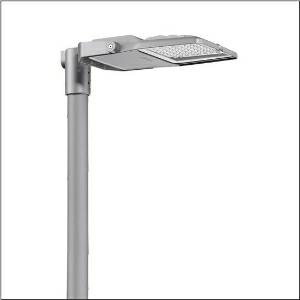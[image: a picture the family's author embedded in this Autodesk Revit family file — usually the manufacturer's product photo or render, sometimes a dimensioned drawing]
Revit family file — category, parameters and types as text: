
# Revit family: floodlight_fl_21_iq_mini___pl64_5xa7771b4e3a_3408
name_source: partatom
category: Lighting Fixtures
units: mm (PartAtom-declared; Revit-internal decimal feet)

## family parameters
Cut with Voids When Loaded = No
Host = Face
Light Source = No
Part Type = Normal
Room Calculation Point = No
Round Connector Dimension = Use Diameter
Shared = No

## types (1)
- --- (1 x LED, 6270 lm, 45.5 W, 4000K)
    Apparent Load = 46 VA
    CIE Flux Codes = 28 80 98 100 100
    Color Rendering = 70
    Color Temperature = 4000K
    Default Elevation = 1800 mm
    Description = Floodlight FL 21 iQ mini, floodlight, primary light control with lens, of PMMA, primary optical cover: protective disc, of toughened safety glass, transparent, light distribution: PL64, light emission: direct distribution, installation type: surface-mounted, LED, High Power LED, rated luminous flux: 6.270lm, luminous efficacy: 138lm/W, light colour: 740, colour temperature: 4000K, control gear: iQ Comfort/DALI, control: Auto-Match, Temp-Guard, Lumen-Switch, Night-Set, Smart-Wire, Light-Fading, Desk-Remote (wireless, voltage-free reading and setting of iQ features in the workshop via application-optimized NFC function/RFID function), optimised constant luminous flux control (CLO 2.0), with terminal, 6-pole, mains connection: 220..240V, AC, 50/60Hz, start of lifetime: 46W, end of service life: 48W, reduction: 22W, luminaire housing, of diecast aluminium, powder-coated, Siteco® metallic grey (DB 702S), corrosivity category C5 mid according to DIN EN ISO 12944, suitable for swimming pools, chlorine-resistant, sealing non-destructively replaceable, please order mast flange separately, mast bracket, of steel, galvanised, powder-coated, Siteco® metallic grey (DB 702S), protection rating (complete): IP66, insulation class (complete): insulation class II (safety insulation), certification: CE, ENEC, VDE, protection symbol: D, impact resistance: IK08, permissible operating ambient temperature: -40..+40°C, permissible operating ambient temperature for outdoor applications: -40..+50°C, standard: DIN EN 12944, LABS conformity tested according to VDMA 24364:2018-05, packaging unit: 1 piece

Light Distribution: PL64
    Height = 70 mm
    Lamp = 1 x LED
    Lamp Light Flux = 6270 lm
    Lamp Power = 45.5 W
    Lamp count = 1
    Length = 485 mm
    Luminous efficacy = 138 lm/W
    Manufacturer = Siteco
    ModVariant = No
    Model = 5XA7771B4E3A
    Number of Poles = 1
    OnlyDefault = Yes
    Power Factor = 1
    Product Name = Floodlight FL 21 iQ mini | PL64
    Product group = floodlight | pylon annexe
    ProductGroupID = 6200
    Protection Class = Protection class II
    Protection Degree = IP 66
    RLX_Detail_Level = 1
    RLX_Emergency_Light_Flux = 0 lm
    RLX_Emergency_Type = 0
    RLX_Emergency_Type_DB = No
    RlxData = <blob elided: 101345 chars, md5=1d864b85>
    Socket = socket
    Standby Power = 0 W
    System Light Flux = 6270 lm
    System Power = 46 W
    Type Comments = factory setting: luminous flux: 100 % | dim-lin: 254 | 463 mA
    Type Image = l_1007125.jpg
    URL = http://relux.com
    VarID = @adj_167046
    Voltage = 0 V
    Weight = 0.00 kg
    Width = 337 mm

## geometry (parser evidence)
native form markers: Blend x4, Sweep x12
no freeform markers — native parametric forms only
